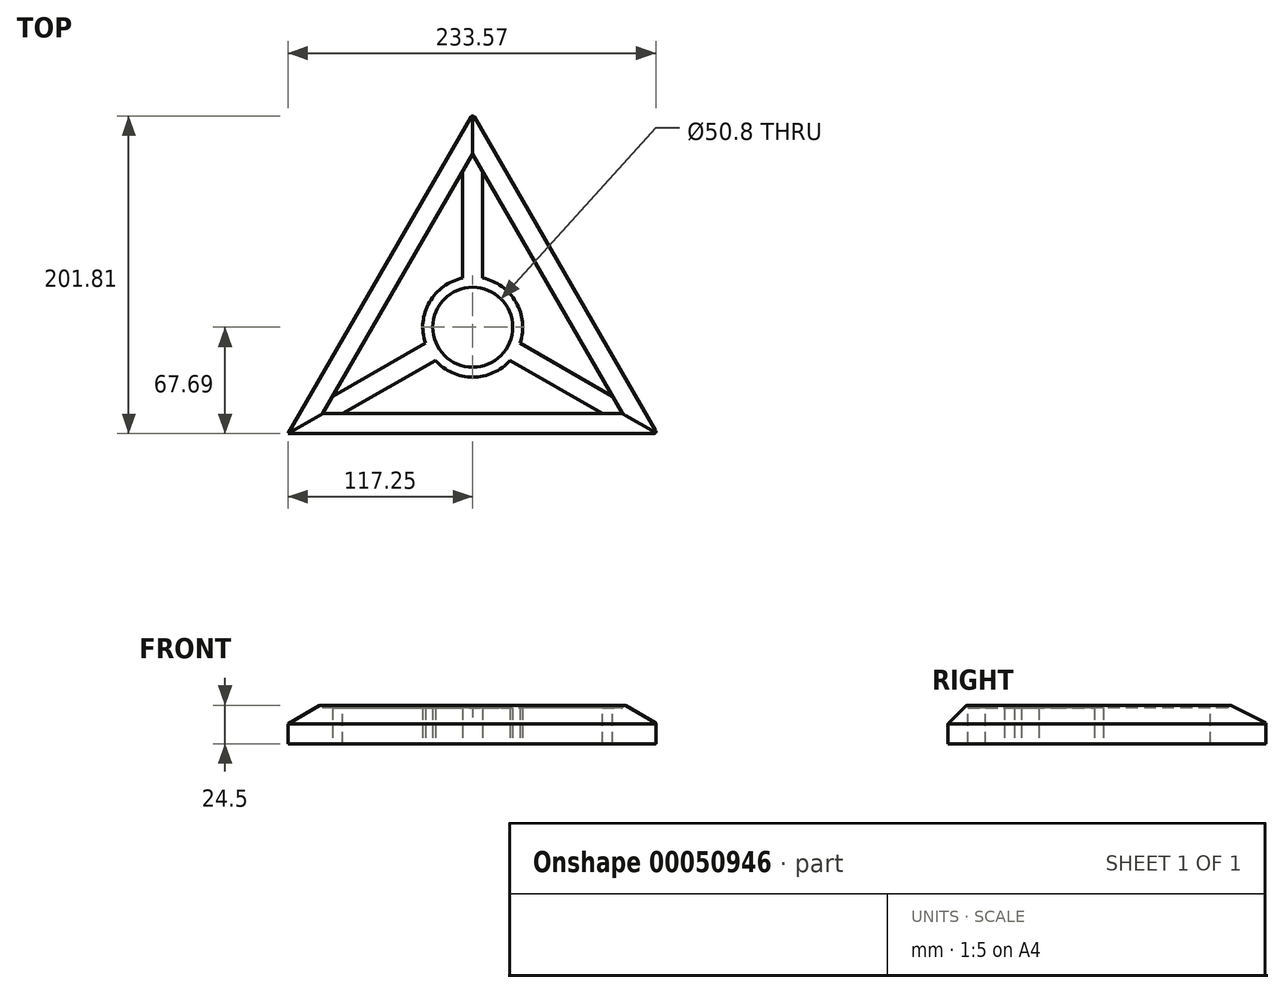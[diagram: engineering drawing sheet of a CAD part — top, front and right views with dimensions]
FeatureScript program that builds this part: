
annotation { "Feature Type Name" : "Feature", "Feature Type Description" : "" }
export const myFeature = defineFeature(function(context is Context, id is Id, definition is map)
    precondition{}
    {
        {
            var Q0;
            Q0=qCreatedBy(makeId("Top.planeOp"),FACE);
            var sketch = newSketch(context, id + "F0", { "sketchPlane" : qUnion([Q0])});
            skLineSegment(sketch, "E0", {"start": v(0, 109.99) * mm, "end": v(-95.25, -55) * mm});
            skLineSegment(sketch, "E1", {"start": v(-95.25, -55) * mm, "end": v(95.25, -55) * mm});
            skLineSegment(sketch, "E2", {"start": v(95.25, -55) * mm, "end": v(0, 109.99) * mm});
            skLineSegment(sketch, "E3", {"start": v(0, 0) * mm, "end": v(-47.62, 27.5) * mm});
            skLineSegment(sketch, "E4.0", {"start": v(0, 135.39) * mm, "end": v(-117.25, -67.7) * mm});
            skLineSegment(sketch, "E4.1", {"start": v(117.25, -67.7) * mm, "end": v(0, 135.39) * mm});
            skLineSegment(sketch, "E4.2", {"start": v(-117.25, -67.7) * mm, "end": v(117.25, -67.7) * mm});
            skSolve(sketch);
        }
        {
            var Q0;
            {var subQ1=sQuery(id+"F0.wireOp",EDGE,"E1");Q0=makeQuery(id+"F0.imprint","IMPRINT",FACE,{"disambiguationData":[TD([[makeQuery(id+"F0.imprint","IMPRINT",EDGE,{"derivedFrom":subQ1}),-1.0]])]});}
            extrude(context, id + "F1", {"entities" : qUnion([Q0]), "depth" : 25.4 * mm});
        }
        {
            var Q0;
            Q0=makeQuery(id+"F1.opExtrude","CAP_VERTEX",VERTEX,{"disambiguationData":[OSD([sQuery(id+"F0.wireOp",EDGE,"E4.0"),sQuery(id+"F0.wireOp",EDGE,"E4.2")])],"isStart":false});
            var Q1;
            Q1=makeQuery(id+"F1.opExtrude","CAP_VERTEX",VERTEX,{"disambiguationData":[OSD([sQuery(id+"F0.wireOp",EDGE,"E0"),sQuery(id+"F0.wireOp",EDGE,"E1")])],"isStart":false});
            var Q2;
            Q2=makeQuery(id+"F1.opExtrude","CAP_VERTEX",VERTEX,{"disambiguationData":[OSD([sQuery(id+"F0.wireOp",EDGE,"E4.0"),sQuery(id+"F0.wireOp",EDGE,"E4.2")])],"isStart":true});
            cPlane(context, id + "F2", {"entities" : qUnion([Q0, Q1, Q2]), "cplaneType" : CPlaneType.THREE_POINT, "offset" : 152.4 * mm, "width" : 152.4 * mm, "height" : 152.4 * mm});
        }
        {
            var Q0;
            Q0=makeQuery(id+"F1.opExtrude","CAP_VERTEX",VERTEX,{"disambiguationData":[OSD([sQuery(id+"F0.wireOp",EDGE,"E4.0"),sQuery(id+"F0.wireOp",EDGE,"E4.1")])],"isStart":false});
            var Q1;
            Q1=makeQuery(id+"F1.opExtrude","CAP_VERTEX",VERTEX,{"disambiguationData":[OSD([sQuery(id+"F0.wireOp",EDGE,"E0"),sQuery(id+"F0.wireOp",EDGE,"E2")])],"isStart":false});
            var Q2;
            Q2=makeQuery(id+"F1.opExtrude","CAP_VERTEX",VERTEX,{"disambiguationData":[OSD([sQuery(id+"F0.wireOp",EDGE,"E0"),sQuery(id+"F0.wireOp",EDGE,"E2")])],"isStart":true});
            cPlane(context, id + "F3", {"entities" : qUnion([Q0, Q1, Q2]), "cplaneType" : CPlaneType.THREE_POINT, "offset" : 152.4 * mm, "width" : 152.4 * mm, "height" : 152.4 * mm});
        }
        {
            var Q0;
            Q0=qCreatedBy(id+"F2.planeOp",FACE);
            var sketch = newSketch(context, id + "F4", { "sketchPlane" : qUnion([Q0])});
            skLineSegment(sketch, "E5", {"start": v(-135.39, 12.7) * mm, "end": v(-135.39, 25.4) * mm});
            skLineSegment(sketch, "E6", {"start": v(-135.39, 25.4) * mm, "end": v(-109.99, 25.4) * mm});
            skLineSegment(sketch, "E7", {"start": v(-109.99, 25.4) * mm, "end": v(-135.39, 12.7) * mm});
            skSolve(sketch);
        }
        {
            var Q0;
            Q0=qCreatedBy(id+"F3.planeOp",FACE);
            var sketch = newSketch(context, id + "F5", { "sketchPlane" : qUnion([Q0])});
            skLineSegment(sketch, "E8", {"start": v(-135.39, 12.7) * mm, "end": v(-135.39, 25.4) * mm});
            skLineSegment(sketch, "E9", {"start": v(-135.39, 25.4) * mm, "end": v(-109.99, 25.4) * mm});
            skLineSegment(sketch, "E10", {"start": v(-109.99, 25.4) * mm, "end": v(-135.39, 12.7) * mm});
            skSolve(sketch);
        }
        {
            var Q0;
            Q0=makeQuery(id+"F1.opExtrude","SWEPT_FACE",FACE,{"disambiguationData":[OSD([sQuery(id+"F0.wireOp",EDGE,"E0")])]});
            var Q1;
            Q1=qCreatedBy(makeId("Origin.pointOp"),VERTEX);
            cPlane(context, id + "F6", {"entities" : qUnion([Q0, Q1]), "cplaneType" : CPlaneType.PLANE_POINT, "offset" : 152.4 * mm, "width" : 152.4 * mm, "height" : 152.4 * mm});
        }
        {
            var Q0;
            Q0=makeQuery(id+"F1.opExtrude","SWEPT_FACE",FACE,{"disambiguationData":[OSD([sQuery(id+"F0.wireOp",EDGE,"E2")])]});
            var Q1;
            Q1=qCreatedBy(makeId("Origin.pointOp"),VERTEX);
            cPlane(context, id + "F7", {"entities" : qUnion([Q0, Q1]), "cplaneType" : CPlaneType.PLANE_POINT, "offset" : 152.4 * mm, "width" : 152.4 * mm, "height" : 152.4 * mm});
        }
        {
            var Q0;
            Q0=makeQuery(id+"F1.opExtrude","SWEPT_FACE",FACE,{"disambiguationData":[OSD([sQuery(id+"F0.wireOp",EDGE,"E1")])]});
            var Q1;
            Q1=qCreatedBy(makeId("Origin.pointOp"),VERTEX);
            cPlane(context, id + "F8", {"entities" : qUnion([Q0, Q1]), "cplaneType" : CPlaneType.PLANE_POINT, "offset" : 152.4 * mm, "width" : 152.4 * mm, "height" : 152.4 * mm});
        }
        {
            var Q0;
            Q0=qCreatedBy(id+"F6.planeOp",FACE);
            var sketch = newSketch(context, id + "F9", { "sketchPlane" : qUnion([Q0])});
            skLineSegment(sketch, "E11.bottom", {"start": v(6.35, 22.86) * mm, "end": v(-6.35, 22.86) * mm});
            skLineSegment(sketch, "E11.top", {"start": v(6.35, 0) * mm, "end": v(-6.35, 0) * mm});
            skLineSegment(sketch, "E11.left", {"start": v(6.35, 22.86) * mm, "end": v(6.35, 0) * mm});
            skLineSegment(sketch, "E11.right", {"start": v(-6.35, 22.86) * mm, "end": v(-6.35, 0) * mm});
            skSolve(sketch);
        }
        {
            var Q0;
            Q0=makeQuery(id+"F9.imprint","IMPRINT",FACE,{"disambiguationData":[TD([[makeQuery(id+"F9.imprint","IMPRINT",EDGE,{"derivedFrom":sQuery(id+"F9.wireOp",EDGE,"E11.bottom")}),1.0]])]});
            extrude(context, id + "F10", {"entities" : qUnion([Q0]), "operationType" : NewBodyOperationType.ADD, "endBound" : BoundingType.UP_TO_NEXT, "depth" : 25.4 * mm});
        }
        {
            var Q0;
            Q0=qCreatedBy(id+"F8.planeOp",FACE);
            var sketch = newSketch(context, id + "F11", { "sketchPlane" : qUnion([Q0])});
            skLineSegment(sketch, "E12.bottom", {"start": v(6.35, 22.86) * mm, "end": v(-6.35, 22.86) * mm});
            skLineSegment(sketch, "E12.top", {"start": v(6.35, 0) * mm, "end": v(-6.35, 0) * mm});
            skLineSegment(sketch, "E12.left", {"start": v(6.35, 22.86) * mm, "end": v(6.35, 0) * mm});
            skLineSegment(sketch, "E12.right", {"start": v(-6.35, 22.86) * mm, "end": v(-6.35, 0) * mm});
            skSolve(sketch);
        }
        {
            var Q0;
            Q0 = qSketchRegion(id + "F11", true);
            extrude(context, id + "F12", {"entities" : qUnion([Q0]), "operationType" : NewBodyOperationType.ADD, "endBound" : BoundingType.UP_TO_NEXT, "depth" : 25.4 * mm});
        }
        {
            var Q0;
            Q0=qCreatedBy(id+"F7.planeOp",FACE);
            var sketch = newSketch(context, id + "F13", { "sketchPlane" : qUnion([Q0])});
            skLineSegment(sketch, "E13.bottom", {"start": v(-6.35, 22.86) * mm, "end": v(6.35, 22.86) * mm});
            skLineSegment(sketch, "E13.top", {"start": v(-6.35, 0) * mm, "end": v(6.35, 0) * mm});
            skLineSegment(sketch, "E13.left", {"start": v(-6.35, 22.86) * mm, "end": v(-6.35, 0) * mm});
            skLineSegment(sketch, "E13.right", {"start": v(6.35, 22.86) * mm, "end": v(6.35, 0) * mm});
            skSolve(sketch);
        }
        {
            var Q0;
            Q0 = qSketchRegion(id + "F13", true);
            var Q1;
            Q1=makeQuery(id+"F1.opExtrude","SWEPT_FACE",FACE,{"disambiguationData":[OSD([sQuery(id+"F0.wireOp",EDGE,"E1")])]});
            extrude(context, id + "F14", {"entities" : qUnion([Q0]), "operationType" : NewBodyOperationType.ADD, "endBound" : BoundingType.UP_TO_SURFACE, "endBoundEntityFace" : qUnion([Q1]), "depth" : 25.4 * mm});
        }
        {
            var Q0;
            Q0 = qSketchRegion(id + "F4", true);
            var Q1;
            Q1=makeQuery(id+"F1.opExtrude","CAP_EDGE",EDGE,{"disambiguationData":[OSD([sQuery(id+"F0.wireOp",EDGE,"E4.0")])],"isStart":false});
            sweep(context, id + "F15", {"operationType" : NewBodyOperationType.REMOVE, "profiles" : qUnion([Q0]), "path" : qUnion([Q1])});
        }
        {
            var Q0;
            Q0=makeQuery(id+"F15.boolean.opBoolean","COPY",FACE,{"derivedFrom":makeQuery(id+"F15.opSweep","CAP_FACE",FACE,{"disambiguationData":[OSD([sQuery(id+"F0.wireOp",EDGE,"E4.0"),sQuery(id+"F0.wireOp",EDGE,"E4.2"),sQuery(id+"F4.wireOp",EDGE,"E5"),sQuery(id+"F4.wireOp",EDGE,"E6"),sQuery(id+"F4.wireOp",EDGE,"E7")])],"isStart":true})});
            var Q1;
            Q1=makeQuery(id+"F1.opExtrude","CAP_EDGE",EDGE,{"disambiguationData":[OSD([sQuery(id+"F0.wireOp",EDGE,"E4.2")])],"isStart":false});
            sweep(context, id + "F16", {"operationType" : NewBodyOperationType.REMOVE, "profiles" : qUnion([Q0]), "path" : qUnion([Q1])});
        }
        {
            var Q0;
            Q0=makeQuery(id+"F5.imprint","IMPRINT",FACE,{"disambiguationData":[TD([[makeQuery(id+"F5.imprint","IMPRINT",EDGE,{"derivedFrom":sQuery(id+"F5.wireOp",EDGE,"E8")}),-1.0]])]});
            var Q1;
            Q1=makeQuery(id+"F1.opExtrude","CAP_EDGE",EDGE,{"disambiguationData":[OSD([sQuery(id+"F0.wireOp",EDGE,"E4.1")])],"isStart":true});
            sweep(context, id + "F17", {"operationType" : NewBodyOperationType.REMOVE, "profiles" : qUnion([Q0]), "path" : qUnion([Q1])});
        }
        {
            var Q0;
            Q0=qCreatedBy(makeId("Top.planeOp"),FACE);
            var sketch = newSketch(context, id + "F18", { "sketchPlane" : qUnion([Q0])});
            skCircle(sketch, "E14", {"center": v(0, 0) * mm, "radius": 31.75 * mm});
            skSolve(sketch);
        }
        {
            var Q0;
            Q0=makeQuery(id+"F18.imprint","IMPRINT",FACE,{"disambiguationData":[TD([[makeQuery(id+"F18.imprint","IMPRINT",EDGE,{"derivedFrom":sQuery(id+"F18.wireOp",EDGE,"E14")}),1.0]])]});
            var Q1;
            Q1=makeQuery(id+"F14.boolean.opBoolean","MERGE",FACE,{"derivedFrom":[makeQuery(id+"F12.boolean.opBoolean","MERGE",FACE,{"derivedFrom":[makeQuery(id+"F10.boolean.opBoolean","MERGE",FACE,{"derivedFrom":[makeQuery(id+"F1.opExtrude","CAP_FACE",FACE,{"disambiguationData":[OSD([sQuery(id+"F0.wireOp",EDGE,"E0"),sQuery(id+"F0.wireOp",EDGE,"E1"),sQuery(id+"F0.wireOp",EDGE,"E2"),sQuery(id+"F0.wireOp",EDGE,"E4.0"),sQuery(id+"F0.wireOp",EDGE,"E4.1"),sQuery(id+"F0.wireOp",EDGE,"E4.2")])],"isStart":false}),makeQuery(id+"F10.opExtrude","SWEPT_FACE",FACE,{"disambiguationData":[OSD([sQuery(id+"F9.wireOp",EDGE,"E11.bottom")])]})]}),makeQuery(id+"F12.opExtrude","SWEPT_FACE",FACE,{"disambiguationData":[OSD([sQuery(id+"F11.wireOp",EDGE,"E12.bottom")])]})]}),makeQuery(id+"F14.opExtrude","SWEPT_FACE",FACE,{"disambiguationData":[OSD([sQuery(id+"F13.wireOp",EDGE,"E13.bottom")])]})]});
            extrude(context, id + "F19", {"entities" : qUnion([Q0]), "operationType" : NewBodyOperationType.ADD, "endBound" : BoundingType.UP_TO_SURFACE, "endBoundEntityFace" : qUnion([Q1]), "depth" : 25.4 * mm});
        }
        {
            var Q0;
            Q0=qCreatedBy(makeId("Top.planeOp"),FACE);
            var sketch = newSketch(context, id + "F20", { "sketchPlane" : qUnion([Q0])});
            skCircle(sketch, "E15", {"center": v(0, 0) * mm, "radius": 25.4 * mm});
            skSolve(sketch);
        }
        {
            var Q0;
            Q0=makeQuery(id+"F20.imprint","IMPRINT",FACE,{"disambiguationData":[TD([[makeQuery(id+"F20.imprint","IMPRINT",EDGE,{"derivedFrom":sQuery(id+"F20.wireOp",EDGE,"E15")}),1.0]])]});
            extrude(context, id + "F21", {"entities" : qUnion([Q0]), "operationType" : NewBodyOperationType.REMOVE, "endBound" : BoundingType.UP_TO_NEXT, "depth" : 25.4 * mm});
        }
        {
            var Q0;
            Q0=makeQuery(id+"F17.boolean.opBoolean","MERGE",EDGE,{"derivedFrom":[makeQuery(id+"F1.opExtrude","CAP_EDGE",EDGE,{"disambiguationData":[OSD([sQuery(id+"F0.wireOp",EDGE,"E2")])],"isStart":false}),makeQuery(id+"F17.opSweep","SWEPT_EDGE",EDGE,{"disambiguationData":[OSD([sQuery(id+"F0.wireOp",EDGE,"E4.1"),sQuery(id+"F5.wireOp",EDGE,"E9"),sQuery(id+"F5.wireOp",EDGE,"E10")])]})]});
            var Q1;
            {var subQ0=sQuery(id+"F0.wireOp",EDGE,"E1");Q1=makeQuery(id+"F16.boolean.opBoolean","MERGE",EDGE,{"derivedFrom":[makeQuery(id+"F1.opExtrude","CAP_EDGE",EDGE,{"disambiguationData":[OSD([subQ0])],"isStart":false}),makeQuery(id+"F16.opSweep","SWEPT_EDGE",EDGE,{"disambiguationData":[OSD([sQuery(id+"F0.wireOp",EDGE,"E0"),subQ0,sQuery(id+"F0.wireOp",EDGE,"E4.0"),sQuery(id+"F0.wireOp",EDGE,"E4.2"),sQuery(id+"F4.wireOp",EDGE,"E6"),sQuery(id+"F4.wireOp",EDGE,"E7")])]})]});}
            var Q2;
            Q2=makeQuery(id+"F15.boolean.opBoolean","MERGE",EDGE,{"derivedFrom":[makeQuery(id+"F1.opExtrude","CAP_EDGE",EDGE,{"disambiguationData":[OSD([sQuery(id+"F0.wireOp",EDGE,"E0")])],"isStart":false}),makeQuery(id+"F15.opSweep","SWEPT_EDGE",EDGE,{"disambiguationData":[OSD([sQuery(id+"F0.wireOp",EDGE,"E4.0"),sQuery(id+"F4.wireOp",EDGE,"E6"),sQuery(id+"F4.wireOp",EDGE,"E7")])]})]});
            fillet(context, id + "F22", {"entities" : qUnion([Q0, Q1, Q2]), "radius" : 0.64 * mm, "allowEdgeOverflow" : false});
        }
        {
            var Q0;
            Q0=makeQuery(id+"F1.opExtrude","SWEPT_EDGE",EDGE,{"disambiguationData":[OSD([sQuery(id+"F0.wireOp",EDGE,"E4.1"),sQuery(id+"F0.wireOp",EDGE,"E4.2")])]});
            var Q1;
            Q1=makeQuery(id+"F1.opExtrude","SWEPT_EDGE",EDGE,{"disambiguationData":[OSD([sQuery(id+"F0.wireOp",EDGE,"E4.0"),sQuery(id+"F0.wireOp",EDGE,"E4.1")])]});
            var Q2;
            Q2=makeQuery(id+"F15.boolean.opBoolean","COPY",EDGE,{"derivedFrom":makeQuery(id+"F1.opExtrude","SWEPT_EDGE",EDGE,{"disambiguationData":[OSD([sQuery(id+"F0.wireOp",EDGE,"E4.0"),sQuery(id+"F0.wireOp",EDGE,"E4.2")])]})});
            fillet(context, id + "F23", {"entities" : qUnion([Q0, Q1, Q2]), "radius" : 1.27 * mm, "tangentPropagation" : true, "allowEdgeOverflow" : false});
        }
    });
